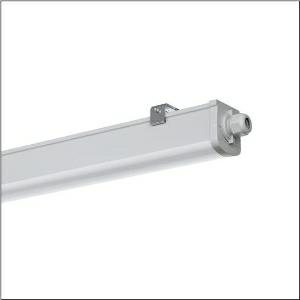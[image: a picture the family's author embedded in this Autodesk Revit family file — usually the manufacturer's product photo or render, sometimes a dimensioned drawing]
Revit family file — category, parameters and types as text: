
# Revit family: monsun_r__31_51fa20dp460b_68f5
name_source: partatom
category: Lighting Fixtures
units: mm (PartAtom-declared; Revit-internal decimal feet)

## family parameters
Cut with Voids When Loaded = No
Host = Face
Light Source = No
Part Type = Normal
Room Calculation Point = No
Round Connector Dimension = Use Diameter
Shared = No

## types (1)
- Monsun® 31 (1 x LED, 6700 lm, 50 W, 4000K)
    Apparent Load = 50 VA
    CIE Flux Codes = 42 72 91 92 100
    Color Rendering = 80
    Color Temperature = 4000K
    Default Elevation = 1800 mm
    Description = Monsun® 31, damp-proof luminaire, primary optical cover: diffuser, of PC, frosted, light emission: direct distribution, primary light characteristic: symmetric, installation type: surface-mounted, LED, rated luminous flux: 6.700lm, luminous efficacy: 134lm/W, light colour: 840, colour temperature: 4000K, control gear: DALI 2, with terminal, 5+1-pole, max. 2.5mm², through-wiring: 3x 2.5mm² + 3x 1.5mm², mains connection: 220..240V, AC, 50/60Hz, rated input power: 50W, housing, luminaire housing, of PC, light grey (RAL 7035), length: 1.458mm, width: 68mm, height: 76mm, protection rating (complete): IP66, insulation class (complete): insulation class II (safety insulation), certification: CE, ENEC, UKCA, protection symbol: D, impact resistance: IK08, permissible operating ambient temperature: -20..+40°C, corresponds to IFS (International Featured Standards) requirements for safety and quality in the food industry, contact your sales advisor before using the luminaires in applications with unclear chemical exposure, large temperature fluctuations or condensation-forming humidity, packaging unit: 1 piece
    Height = 77 mm
    Lamp = 1 x LED
    Lamp Light Flux = 6700 lm
    Lamp Power = 50 W
    Lamp count = 1
    Length = 1518 mm
    Luminous efficacy = 134 lm/W
    Manufacturer = Siteco
    ModVariant = No
    Model = 51FA20DP460B
    Mounting Place = Ceiling
    Mounting Type = Surface mounted
    Number of Poles = 1
    OnlyDefault = Yes
    Power Factor = 1
    Product Name = Monsun® 31
    Product group = damp-proof luminaire
    ProductGroupID = 301
    Protection Class = Protection class II
    Protection Degree = IP 66
    RLX_Detail_Level = 1
    RLX_Emergency_Light_Flux = 0 lm
    RLX_Emergency_Type = 0
    RLX_Emergency_Type_DB = No
    RlxData = <blob elided: 33137 chars, md5=d5fe3cd4>
    Socket = socket
    Standby Power = 0 W
    System Light Flux = 6700 lm
    System Power = 50 W
    Type Comments = Product without accessories
    Type Image = l_1006174.jpg
    URL = http://relux.com
    VarID = ---
    Voltage = 0 V
    Weight = 0.00 kg
    Width = 69 mm

## geometry (parser evidence)
native form markers: Blend x4, Sweep x13
no freeform markers — native parametric forms only
